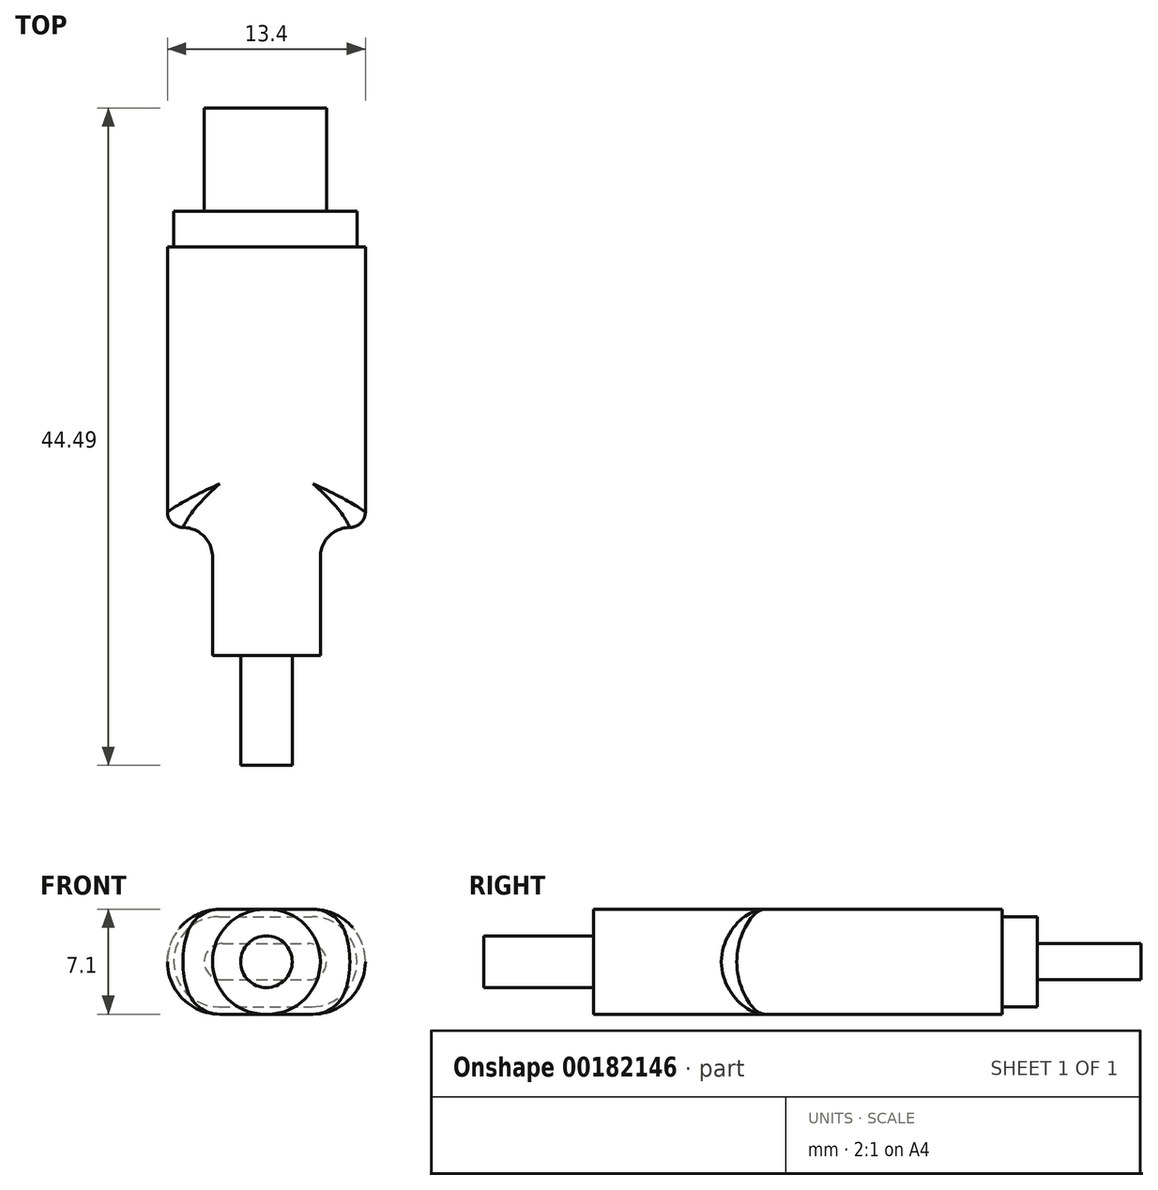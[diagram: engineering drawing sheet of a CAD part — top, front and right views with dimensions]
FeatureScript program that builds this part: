
annotation { "Feature Type Name" : "Feature", "Feature Type Description" : "" }
export const myFeature = defineFeature(function(context is Context, id is Id, definition is map)
    precondition{}
    {
        {
            var Q0;
            Q0=qCreatedBy(makeId("Top.planeOp"),FACE);
            var sketch = newSketch(context, id + "F0", { "sketchPlane" : qUnion([Q0])});
            skLineSegment(sketch, "E0.top", {"start": v(5.65, -9.5) * mm, "end": v(5.65, -9.5) * mm});
            skLineSegment(sketch, "E0.left", {"start": v(6.7, 9.5) * mm, "end": v(6.7, -8.45) * mm});
            skLineSegment(sketch, "E0.right", {"start": v(-6.7, 9.5) * mm, "end": v(-6.7, -8.45) * mm});
            skPoint(sketch, "E0.middle", {"position": v(0, 0) * mm});
            skLineSegment(sketch, "E1.bottom", {"start": v(-6.27, 11.9) * mm, "end": v(-4.2, 11.9) * mm});
            skPoint(sketch, "E1.middle", {"position": v(0, 10.7) * mm});
            skPoint(sketch, "E1.middle.positionSnap0", {"position": v(0, 9.5) * mm});
            skPoint(sketch, "E1.centerSnap0", {"position": v(0, 9.5) * mm});
            skLineSegment(sketch, "E2.top", {"start": v(4.07, 18.9) * mm, "end": v(-4.2, 18.9) * mm});
            skLineSegment(sketch, "E2.left", {"start": v(4.07, 11.9) * mm, "end": v(4.07, 18.9) * mm});
            skLineSegment(sketch, "E2.right", {"start": v(-4.2, 11.9) * mm, "end": v(-4.2, 18.9) * mm});
            skPoint(sketch, "E2.middle", {"position": v(-0.07, 15.4) * mm});
            skPoint(sketch, "E2.middle.positionSnap0", {"position": v(-0.07, 11.9) * mm});
            skPoint(sketch, "E2.centerSnap0", {"position": v(-0.07, 11.9) * mm});
            skLineSegment(sketch, "E3.bottom", {"start": v(3.65, -18.15) * mm, "end": v(1.75, -18.15) * mm});
            skLineSegment(sketch, "E3.left", {"start": v(3.65, -18.15) * mm, "end": v(3.65, -11.5) * mm});
            skLineSegment(sketch, "E3.right", {"start": v(-3.65, -18.15) * mm, "end": v(-3.65, -11.5) * mm});
            skPoint(sketch, "E3.middle", {"position": v(0, -13.83) * mm});
            skPoint(sketch, "E3.middle.positionSnap0", {"position": v(0, -9.5) * mm});
            skPoint(sketch, "E3.centerSnap0", {"position": v(0, -9.5) * mm});
            skLineSegment(sketch, "E4.bottom", {"start": v(1.75, -25.59) * mm, "end": v(-1.75, -25.59) * mm});
            skLineSegment(sketch, "E4.left", {"start": v(1.75, -25.59) * mm, "end": v(1.75, -18.15) * mm});
            skLineSegment(sketch, "E4.right", {"start": v(-1.75, -25.59) * mm, "end": v(-1.75, -18.15) * mm});
            skPoint(sketch, "E4.middle", {"position": v(0, -21.87) * mm});
            skLineSegment(sketch, "E5.trimOffspring", {"start": v(-5.65, -9.5) * mm, "end": v(-5.65, -9.5) * mm});
            skPoint(sketch, "E6.visualSharp", {"position": v(-3.65, -9.5) * mm});
            skArc(sketch, "E6.filletArc", {"start": v(-3.65, -11.5) * mm, "mid": v(-4.24, -10.09) * mm, "end": v(-5.65, -9.5) * mm});
            skPoint(sketch, "E7.visualSharp", {"position": v(3.65, -9.5) * mm});
            skArc(sketch, "E7.filletArc", {"start": v(5.65, -9.5) * mm, "mid": v(4.24, -10.09) * mm, "end": v(3.65, -11.5) * mm});
            skLineSegment(sketch, "E8.trimOffspring", {"start": v(4.07, 11.9) * mm, "end": v(6.13, 11.9) * mm});
            skLineSegment(sketch, "E9.trimOffspring", {"start": v(-1.75, -18.15) * mm, "end": v(-3.65, -18.15) * mm});
            skLineSegment(sketch, "E10", {"start": v(-4.2, 11.9) * mm, "end": v(4.07, 11.9) * mm});
            skLineSegment(sketch, "E11", {"start": v(-1.75, -18.15) * mm, "end": v(1.75, -18.15) * mm});
            skLineSegment(sketch, "E12", {"start": v(6.7, 9.5) * mm, "end": v(6.13, 9.5) * mm});
            skLineSegment(sketch, "E13", {"start": v(6.13, 9.5) * mm, "end": v(6.13, 11.9) * mm});
            skLineSegment(sketch, "E14", {"start": v(-6.27, 11.9) * mm, "end": v(-6.27, 9.5) * mm});
            skLineSegment(sketch, "E15", {"start": v(-6.27, 9.5) * mm, "end": v(-6.7, 9.5) * mm});
            skLineSegment(sketch, "E16", {"start": v(6.13, 9.5) * mm, "end": v(-6.27, 9.5) * mm});
            skPoint(sketch, "E17.visualSharp", {"position": v(6.7, -9.5) * mm});
            skArc(sketch, "E17.filletArc", {"start": v(5.65, -9.5) * mm, "mid": v(6.4, -9.2) * mm, "end": v(6.7, -8.45) * mm});
            skPoint(sketch, "E18.visualSharp", {"position": v(-6.7, -9.5) * mm});
            skArc(sketch, "E18.filletArc", {"start": v(-6.7, -8.45) * mm, "mid": v(-6.4, -9.2) * mm, "end": v(-5.65, -9.5) * mm});
            skSolve(sketch);
        }
        {
            var Q0;
            Q0=makeQuery(id+"F0.imprint","IMPRINT",FACE,{"disambiguationData":[TD([[makeQuery(id+"F0.imprint","IMPRINT",EDGE,{"derivedFrom":sQuery(id+"F0.wireOp",EDGE,"E0.top")}),-1.0]])]});
            var Q1;
            Q1=makeQuery(id+"F0.imprint","IMPRINT",FACE,{"disambiguationData":[TD([[makeQuery(id+"F0.imprint","IMPRINT",EDGE,{"derivedFrom":sQuery(id+"F0.wireOp",EDGE,"E0.left")}),-1.0]])]});
            extrude(context, id + "F1", {"entities" : qUnion([Q0, Q1]), "endBound" : BoundingType.SYMMETRIC, "depth" : 7.1 * mm});
        }
        {
            var Q0;
            Q0=makeQuery(id+"F0.imprint","IMPRINT",FACE,{"disambiguationData":[TD([[makeQuery(id+"F0.imprint","IMPRINT",EDGE,{"derivedFrom":sQuery(id+"F0.wireOp",EDGE,"E1.bottom")}),-1.0]])]});
            extrude(context, id + "F2", {"entities" : qUnion([Q0]), "operationType" : NewBodyOperationType.ADD, "endBound" : BoundingType.SYMMETRIC, "depth" : 6.1 * mm});
        }
        {
            var Q0;
            Q0=makeQuery(id+"F0.imprint","IMPRINT",FACE,{"disambiguationData":[TD([[makeQuery(id+"F0.imprint","IMPRINT",EDGE,{"derivedFrom":sQuery(id+"F0.wireOp",EDGE,"E2.top")}),1.0]])]});
            extrude(context, id + "F3", {"entities" : qUnion([Q0]), "operationType" : NewBodyOperationType.ADD, "endBound" : BoundingType.SYMMETRIC, "depth" : 2.45 * mm});
        }
        {
            var Q0;
            Q0=makeQuery(id+"F0.imprint","IMPRINT",FACE,{"disambiguationData":[TD([[makeQuery(id+"F0.imprint","IMPRINT",EDGE,{"derivedFrom":sQuery(id+"F0.wireOp",EDGE,"E4.bottom")}),-1.0]])]});
            extrude(context, id + "F4", {"entities" : qUnion([Q0]), "operationType" : NewBodyOperationType.ADD, "endBound" : BoundingType.SYMMETRIC, "depth" : 3.5 * mm});
        }
        {
            var Q0;
            Q0=makeQuery(id+"F3.opExtrude","CAP_EDGE",EDGE,{"disambiguationData":[OSD([sQuery(id+"F0.wireOp",EDGE,"E2.left")])],"isStart":true});
            var Q1;
            Q1=makeQuery(id+"F3.opExtrude","CAP_EDGE",EDGE,{"disambiguationData":[OSD([sQuery(id+"F0.wireOp",EDGE,"E2.left")])],"isStart":false});
            var Q2;
            Q2=makeQuery(id+"F3.opExtrude","CAP_EDGE",EDGE,{"disambiguationData":[OSD([sQuery(id+"F0.wireOp",EDGE,"E2.right")])],"isStart":true});
            var Q3;
            Q3=makeQuery(id+"F3.opExtrude","CAP_EDGE",EDGE,{"disambiguationData":[OSD([sQuery(id+"F0.wireOp",EDGE,"E2.right")])],"isStart":false});
            fillet(context, id + "F5", {"entities" : qUnion([Q0, Q1, Q2, Q3]), "radius" : (2.45 / 2) * mm, "tangentPropagation" : true, "allowEdgeOverflow" : false});
        }
        {
            var Q0;
            Q0=makeQuery(id+"F2.opExtrude","CAP_EDGE",EDGE,{"disambiguationData":[OSD([sQuery(id+"F0.wireOp",EDGE,"E13")])],"isStart":false});
            var Q1;
            Q1=makeQuery(id+"F2.opExtrude","CAP_EDGE",EDGE,{"disambiguationData":[OSD([sQuery(id+"F0.wireOp",EDGE,"E13")])],"isStart":true});
            var Q2;
            Q2=makeQuery(id+"F2.opExtrude","CAP_EDGE",EDGE,{"disambiguationData":[OSD([sQuery(id+"F0.wireOp",EDGE,"E14")])],"isStart":true});
            var Q3;
            Q3=makeQuery(id+"F2.opExtrude","CAP_EDGE",EDGE,{"disambiguationData":[OSD([sQuery(id+"F0.wireOp",EDGE,"E14")])],"isStart":false});
            fillet(context, id + "F6", {"entities" : qUnion([Q0, Q1, Q2, Q3]), "radius" : (6.1 / 2) * mm, "tangentPropagation" : true, "allowEdgeOverflow" : false});
        }
        {
            var Q0;
            Q0=makeQuery(id+"F1.opExtrude","CAP_EDGE",EDGE,{"disambiguationData":[OSD([sQuery(id+"F0.wireOp",EDGE,"E0.left")])],"isStart":false});
            var Q1;
            Q1=makeQuery(id+"F1.opExtrude","CAP_EDGE",EDGE,{"disambiguationData":[OSD([sQuery(id+"F0.wireOp",EDGE,"E0.left")])],"isStart":true});
            var Q2;
            Q2=makeQuery(id+"F1.opExtrude","CAP_EDGE",EDGE,{"disambiguationData":[OSD([sQuery(id+"F0.wireOp",EDGE,"E0.right")])],"isStart":false});
            var Q3;
            Q3=makeQuery(id+"F1.opExtrude","CAP_EDGE",EDGE,{"disambiguationData":[OSD([sQuery(id+"F0.wireOp",EDGE,"E0.right")])],"isStart":true});
            fillet(context, id + "F7", {"entities" : qUnion([Q0, Q1, Q2, Q3]), "radius" : (7.1 / 2) * mm, "tangentPropagation" : true, "allowEdgeOverflow" : false});
        }
        {
            var Q0;
            Q0=makeQuery(id+"F4.opExtrude","CAP_EDGE",EDGE,{"disambiguationData":[OSD([sQuery(id+"F0.wireOp",EDGE,"E4.left")])],"isStart":false});
            var Q1;
            Q1=makeQuery(id+"F4.opExtrude","CAP_EDGE",EDGE,{"disambiguationData":[OSD([sQuery(id+"F0.wireOp",EDGE,"E4.left")])],"isStart":true});
            var Q2;
            Q2=makeQuery(id+"F4.opExtrude","CAP_EDGE",EDGE,{"disambiguationData":[OSD([sQuery(id+"F0.wireOp",EDGE,"E4.right")])],"isStart":true});
            var Q3;
            Q3=makeQuery(id+"F4.opExtrude","CAP_EDGE",EDGE,{"disambiguationData":[OSD([sQuery(id+"F0.wireOp",EDGE,"E4.right")])],"isStart":false});
            fillet(context, id + "F8", {"entities" : qUnion([Q0, Q1, Q2, Q3]), "radius" : (3.5 / 2) * mm, "tangentPropagation" : true, "allowEdgeOverflow" : false});
        }
    });
